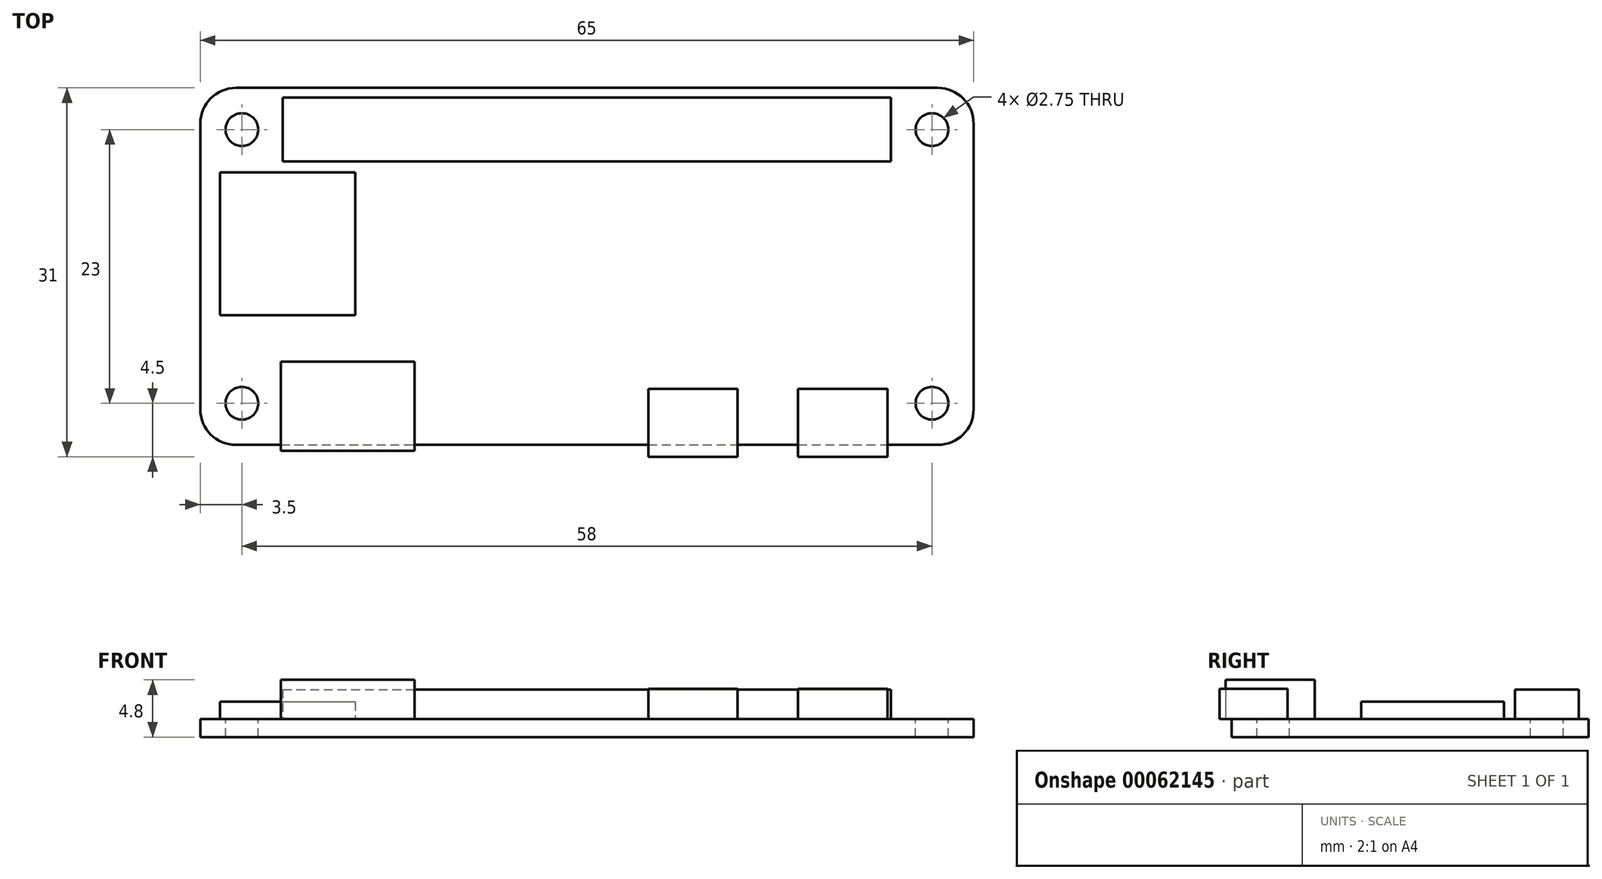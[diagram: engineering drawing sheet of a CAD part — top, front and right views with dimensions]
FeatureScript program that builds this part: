
annotation { "Feature Type Name" : "Feature", "Feature Type Description" : "" }
export const myFeature = defineFeature(function(context is Context, id is Id, definition is map)
    precondition{}
    {
        {
            var Q0;
            Q0=qCreatedBy(makeId("Top.planeOp"),FACE);
            var sketch = newSketch(context, id + "F0", { "sketchPlane" : qUnion([Q0])});
            skLineSegment(sketch, "E0.bottom", {"start": v(-32.5, 15) * mm, "end": v(32.5, 15) * mm});
            skLineSegment(sketch, "E0.top", {"start": v(-32.5, -15) * mm, "end": v(32.5, -15) * mm});
            skLineSegment(sketch, "E0.left", {"start": v(-32.5, 15) * mm, "end": v(-32.5, -15) * mm});
            skLineSegment(sketch, "E0.right", {"start": v(32.5, 15) * mm, "end": v(32.5, -15) * mm});
            skSolve(sketch);
        }
        {
            var Q0;
            Q0=makeQuery(id+"F0.imprint","IMPRINT",FACE,{"disambiguationData":[TD([[makeQuery(id+"F0.imprint","IMPRINT",EDGE,{"derivedFrom":sQuery(id+"F0.wireOp",EDGE,"E0.bottom")}),-1.0]])]});
            extrude(context, id + "F1", {"entities" : qUnion([Q0]), "depth" : 1.5 * mm});
        }
        {
            var Q0;
            Q0=makeQuery(id+"F1.opExtrude","CAP_FACE",FACE,{"disambiguationData":[OSD([sQuery(id+"F0.wireOp",EDGE,"E0.bottom"),sQuery(id+"F0.wireOp",EDGE,"E0.top"),sQuery(id+"F0.wireOp",EDGE,"E0.left"),sQuery(id+"F0.wireOp",EDGE,"E0.right")])],"isStart":false});
            var sketch = newSketch(context, id + "F2", { "sketchPlane" : qUnion([Q0])});
            skPoint(sketch, "E1", {"position": v(-29, 11.5) * mm});
            skPoint(sketch, "E2", {"position": v(-29, -11.5) * mm});
            skPoint(sketch, "E3", {"position": v(29, -11.5) * mm});
            skPoint(sketch, "E4", {"position": v(29, 11.5) * mm});
            skSolve(sketch);
        }
        {
            var Q0;
            Q0=sQuery(id+"F2.wireOp",VERTEX,"E1");
            var Q1;
            Q1=sQuery(id+"F2.wireOp",VERTEX,"E2");
            var Q2;
            Q2=sQuery(id+"F2.wireOp",VERTEX,"E3");
            var Q3;
            Q3=sQuery(id+"F2.wireOp",VERTEX,"E4");
            var Q4;
            Q4=makeQuery(id+"F1.opExtrude","SWEPT_BODY",BODY,{"disambiguationData":[OSD([sQuery(id+"F0.wireOp",EDGE,"E0.bottom"),sQuery(id+"F0.wireOp",EDGE,"E0.top"),sQuery(id+"F0.wireOp",EDGE,"E0.left"),sQuery(id+"F0.wireOp",EDGE,"E0.right")])]});
            hole(context, id + "F3", {"style" : HoleStyle.SIMPLE, "holeDiameter" : 2.75 * mm, "endStyle" : HoleEndStyle.THROUGH, "locations" : qUnion([Q0, Q1, Q2, Q3]), "scope" : qUnion([Q4])});
        }
        {
            var Q0;
            Q0=makeQuery(id+"F1.opExtrude","SWEPT_EDGE",EDGE,{"disambiguationData":[OSD([sQuery(id+"F0.wireOp",EDGE,"E0.top"),sQuery(id+"F0.wireOp",EDGE,"E0.left")])]});
            var Q1;
            Q1=makeQuery(id+"F1.opExtrude","SWEPT_EDGE",EDGE,{"disambiguationData":[OSD([sQuery(id+"F0.wireOp",EDGE,"E0.bottom"),sQuery(id+"F0.wireOp",EDGE,"E0.left")])]});
            var Q2;
            Q2=makeQuery(id+"F1.opExtrude","SWEPT_EDGE",EDGE,{"disambiguationData":[OSD([sQuery(id+"F0.wireOp",EDGE,"E0.top"),sQuery(id+"F0.wireOp",EDGE,"E0.right")])]});
            var Q3;
            Q3=makeQuery(id+"F1.opExtrude","SWEPT_EDGE",EDGE,{"disambiguationData":[OSD([sQuery(id+"F0.wireOp",EDGE,"E0.bottom"),sQuery(id+"F0.wireOp",EDGE,"E0.right")])]});
            fillet(context, id + "F4", {"entities" : qUnion([Q0, Q1, Q2, Q3]), "radius" : 3 * mm, "tangentPropagation" : true, "allowEdgeOverflow" : false});
        }
        {
            var Q0;
            Q0=makeQuery(id+"F1.opExtrude","CAP_FACE",FACE,{"disambiguationData":[OSD([sQuery(id+"F0.wireOp",EDGE,"E0.bottom"),sQuery(id+"F0.wireOp",EDGE,"E0.top"),sQuery(id+"F0.wireOp",EDGE,"E0.left"),sQuery(id+"F0.wireOp",EDGE,"E0.right")])],"isStart":false});
            var sketch = newSketch(context, id + "F5", { "sketchPlane" : qUnion([Q0])});
            skLineSegment(sketch, "E5.bottom", {"start": v(-25.72, -15.5) * mm, "end": v(-14.48, -15.5) * mm});
            skLineSegment(sketch, "E5.top", {"start": v(-25.72, -8) * mm, "end": v(-14.47, -8) * mm});
            skLineSegment(sketch, "E5.left", {"start": v(-25.73, -15.5) * mm, "end": v(-25.72, -8) * mm});
            skLineSegment(sketch, "E5.right", {"start": v(-14.48, -15.5) * mm, "end": v(-14.48, -8) * mm});
            skLineSegment(sketch, "E6.bottom", {"start": v(5.15, -16) * mm, "end": v(12.65, -16) * mm});
            skLineSegment(sketch, "E6.top", {"start": v(5.15, -10.3) * mm, "end": v(12.65, -10.3) * mm});
            skLineSegment(sketch, "E6.left", {"start": v(5.15, -16) * mm, "end": v(5.15, -10.3) * mm});
            skLineSegment(sketch, "E6.right", {"start": v(12.65, -16) * mm, "end": v(12.65, -10.3) * mm});
            skLineSegment(sketch, "E7.bottom", {"start": v(17.75, -16) * mm, "end": v(25.25, -16) * mm});
            skLineSegment(sketch, "E7.top", {"start": v(17.75, -10.3) * mm, "end": v(25.25, -10.3) * mm});
            skLineSegment(sketch, "E7.left", {"start": v(17.75, -16) * mm, "end": v(17.75, -10.3) * mm});
            skLineSegment(sketch, "E7.right", {"start": v(25.25, -16) * mm, "end": v(25.25, -10.3) * mm});
            skLineSegment(sketch, "E8", {"start": v(21.5, -10.3) * mm, "end": v(21.5, -16) * mm, "construction": true});
            skLineSegment(sketch, "E9", {"start": v(8.9, -10.3) * mm, "end": v(8.9, -16) * mm, "construction": true});
            skLineSegment(sketch, "E10", {"start": v(-20.1, -8) * mm, "end": v(-20.1, -15.5) * mm, "construction": true});
            skLineSegment(sketch, "E11.bottom", {"start": v(-30.85, 7.9) * mm, "end": v(-19.46, 7.9) * mm});
            skLineSegment(sketch, "E11.top", {"start": v(-30.85, -4.1) * mm, "end": v(-19.46, -4.1) * mm});
            skLineSegment(sketch, "E11.left", {"start": v(-30.85, 7.9) * mm, "end": v(-30.85, -4.1) * mm});
            skLineSegment(sketch, "E11.right", {"start": v(-19.46, 7.9) * mm, "end": v(-19.46, -4.1) * mm});
            skLineSegment(sketch, "E12", {"start": v(-30.85, 1.9) * mm, "end": v(-19.46, 1.9) * mm, "construction": true});
            skLineSegment(sketch, "E13.bottom", {"start": v(-25.56, 14.19) * mm, "end": v(25.56, 14.19) * mm});
            skLineSegment(sketch, "E13.top", {"start": v(-25.56, 8.81) * mm, "end": v(25.56, 8.81) * mm});
            skLineSegment(sketch, "E13.left", {"start": v(-25.56, 14.19) * mm, "end": v(-25.56, 8.81) * mm});
            skLineSegment(sketch, "E13.right", {"start": v(25.56, 14.19) * mm, "end": v(25.56, 8.81) * mm});
            skLineSegment(sketch, "E14", {"start": v(0, 14.19) * mm, "end": v(0, 8.81) * mm, "construction": true});
            skLineSegment(sketch, "E15", {"start": v(-25.56, 11.5) * mm, "end": v(25.56, 11.5) * mm, "construction": true});
            skCircle(sketch, "E16.0", {"center": v(-29, 11.5) * mm, "radius": 1.37 * mm});
            skSolve(sketch);
        }
        {
            var Q0;
            {var subQ0=sQuery(id+"F5.wireOp",EDGE,"E6.top");Q0=makeQuery(id+"F5.imprint","IMPRINT",FACE,{"disambiguationData":[TD([[makeQuery(id+"F5.imprint","IMPRINT",EDGE,{"derivedFrom":subQ0}),-1.0]])]});}
            var Q1;
            {var subQ0=sQuery(id+"F5.wireOp",EDGE,"E6.bottom");Q1=makeQuery(id+"F5.imprint","IMPRINT",FACE,{"disambiguationData":[TD([[makeQuery(id+"F5.imprint","IMPRINT",EDGE,{"derivedFrom":subQ0}),1.0]])]});}
            var Q2;
            {var subQ0=sQuery(id+"F5.wireOp",EDGE,"E7.bottom");Q2=makeQuery(id+"F5.imprint","IMPRINT",FACE,{"disambiguationData":[TD([[makeQuery(id+"F5.imprint","IMPRINT",EDGE,{"derivedFrom":subQ0}),1.0]])]});}
            var Q3;
            {var subQ0=sQuery(id+"F5.wireOp",EDGE,"E7.top");Q3=makeQuery(id+"F5.imprint","IMPRINT",FACE,{"disambiguationData":[TD([[makeQuery(id+"F5.imprint","IMPRINT",EDGE,{"derivedFrom":subQ0}),-1.0]])]});}
            extrude(context, id + "F6", {"entities" : qUnion([Q0, Q1, Q2, Q3]), "operationType" : NewBodyOperationType.ADD, "depth" : 2.55 * mm});
        }
        {
            var Q0;
            {var subQ0=sQuery(id+"F5.wireOp",EDGE,"E5.top");Q0=makeQuery(id+"F5.imprint","IMPRINT",FACE,{"disambiguationData":[TD([[makeQuery(id+"F5.imprint","IMPRINT",EDGE,{"derivedFrom":subQ0}),-1.0]])]});}
            var Q1;
            {var subQ0=sQuery(id+"F5.wireOp",EDGE,"E5.bottom");Q1=makeQuery(id+"F5.imprint","IMPRINT",FACE,{"disambiguationData":[TD([[makeQuery(id+"F5.imprint","IMPRINT",EDGE,{"derivedFrom":subQ0}),1.0]])]});}
            extrude(context, id + "F7", {"entities" : qUnion([Q0, Q1]), "operationType" : NewBodyOperationType.ADD, "depth" : 3.3 * mm});
        }
        {
            var Q0;
            Q0=makeQuery(id+"F5.imprint","IMPRINT",FACE,{"disambiguationData":[TD([[makeQuery(id+"F5.imprint","IMPRINT",EDGE,{"derivedFrom":sQuery(id+"F5.wireOp",EDGE,"E11.bottom")}),-1.0]])]});
            extrude(context, id + "F8", {"entities" : qUnion([Q0]), "operationType" : NewBodyOperationType.ADD, "depth" : 1.47 * mm});
        }
        {
            var Q0;
            Q0=makeQuery(id+"F5.imprint","IMPRINT",FACE,{"disambiguationData":[TD([[makeQuery(id+"F5.imprint","IMPRINT",EDGE,{"derivedFrom":sQuery(id+"F5.wireOp",EDGE,"E13.bottom")}),-1.0]])]});
            extrude(context, id + "F9", {"entities" : qUnion([Q0]), "operationType" : NewBodyOperationType.ADD, "depth" : 2.5 * mm});
        }
    });
